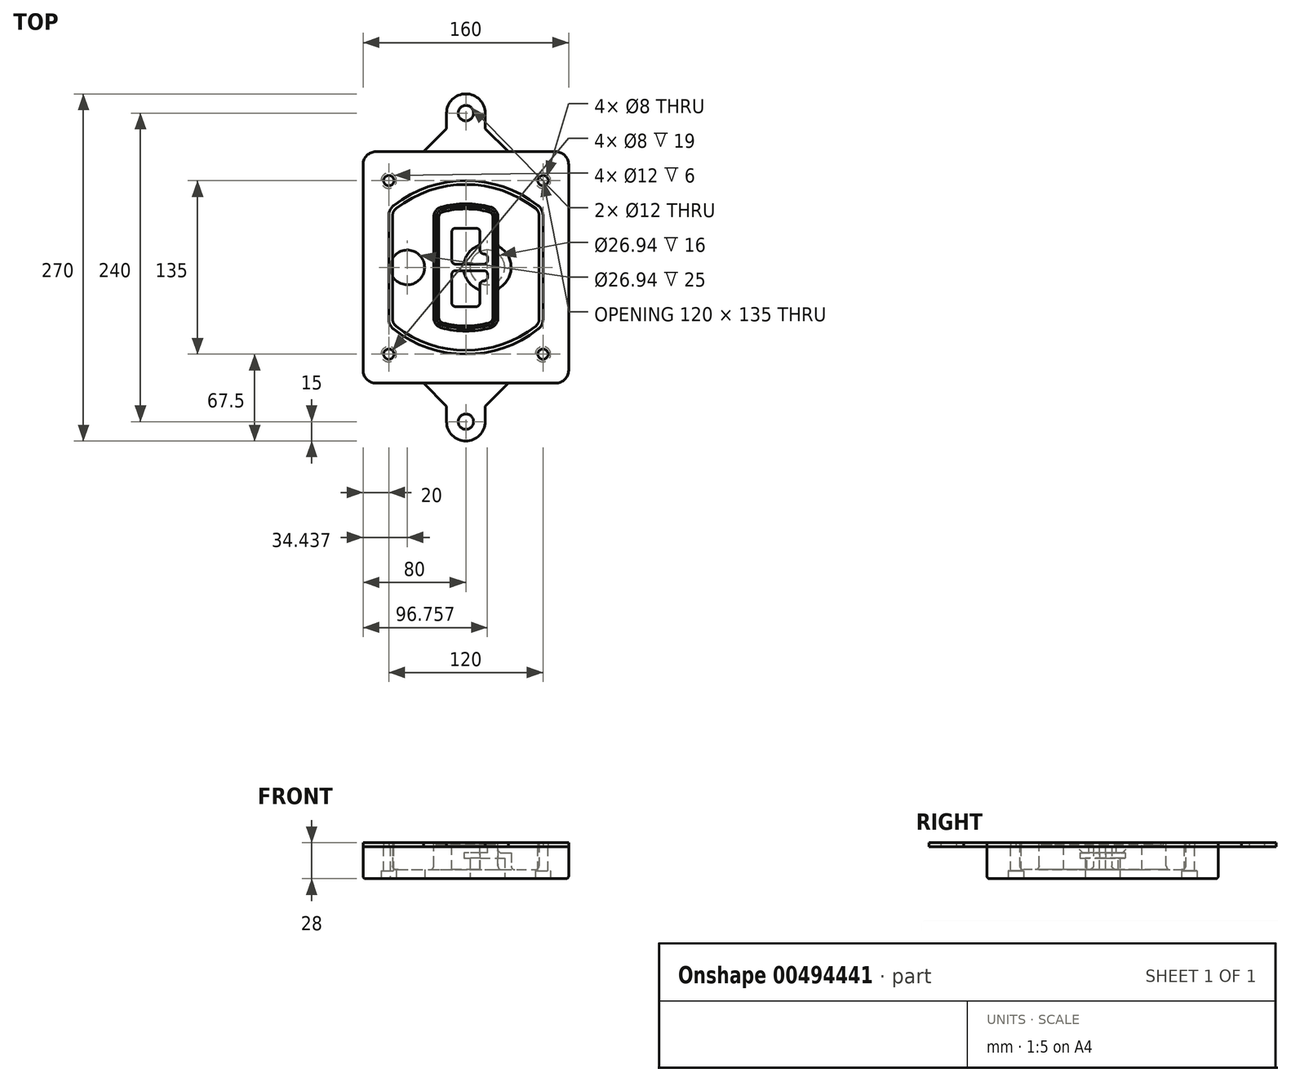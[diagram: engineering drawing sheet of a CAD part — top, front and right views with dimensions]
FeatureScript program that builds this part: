
annotation { "Feature Type Name" : "Feature", "Feature Type Description" : "" }
export const myFeature = defineFeature(function(context is Context, id is Id, definition is map)
    precondition{}
    {
        {
            var Q0;
            Q0=qCreatedBy(makeId("Top.planeOp"),FACE);
            var sketch = newSketch(context, id + "F0", { "sketchPlane" : qUnion([Q0])});
            skPoint(sketch, "E0.rect.middle", {"position": v(0, 0) * mm});
            skLineSegment(sketch, "E1.bottom", {"start": v(-70, -90) * mm, "end": v(70, -90) * mm});
            skLineSegment(sketch, "E1.top", {"start": v(-70, 90) * mm, "end": v(70, 90) * mm});
            skLineSegment(sketch, "E1.left", {"start": v(-80, -80) * mm, "end": v(-80, 80) * mm});
            skLineSegment(sketch, "E1.right", {"start": v(80, -80) * mm, "end": v(80, 80) * mm});
            skLineSegment(sketch, "E2", {"start": v(-80, 90) * mm, "end": v(80, -90) * mm, "construction": true});
            skLineSegment(sketch, "E3", {"start": v(80, 90) * mm, "end": v(-80, -90) * mm, "construction": true});
            skCircle(sketch, "E4", {"center": v(-60, 67.5) * mm, "radius": 4 * mm});
            skCircle(sketch, "E5", {"center": v(60, 67.5) * mm, "radius": 4 * mm});
            skCircle(sketch, "E6", {"center": v(60, -67.5) * mm, "radius": 4 * mm});
            skCircle(sketch, "E7", {"center": v(-60, -67.5) * mm, "radius": 4 * mm});
            skLineSegment(sketch, "E8", {"start": v(-60, 67.5) * mm, "end": v(60, 67.5) * mm, "construction": true});
            skLineSegment(sketch, "E9", {"start": v(60, 67.5) * mm, "end": v(60, -67.5) * mm, "construction": true});
            skLineSegment(sketch, "E10", {"start": v(60, -67.5) * mm, "end": v(-60, -67.5) * mm, "construction": true});
            skLineSegment(sketch, "E11", {"start": v(-60, -67.5) * mm, "end": v(-60, 67.5) * mm, "construction": true});
            skLineSegment(sketch, "E12", {"start": v(-60, 40.3) * mm, "end": v(-60, -40.3) * mm});
            skLineSegment(sketch, "E13", {"start": v(60, 40.3) * mm, "end": v(60, -40.3) * mm});
            skArc(sketch, "E14", {"start": v(56.15, 48.18) * mm, "mid": v(0, 67.5) * mm, "end": v(-56.15, 48.18) * mm});
            skArc(sketch, "E15", {"start": v(-56.15, -48.18) * mm, "mid": v(0, -67.5) * mm, "end": v(56.15, -48.18) * mm});
            skLineSegment(sketch, "E16", {"start": v(-60, 0) * mm, "end": v(60, 0) * mm, "construction": true});
            skPoint(sketch, "E17.visualSharp", {"position": v(-60, -45) * mm});
            skArc(sketch, "E17.filletArc", {"start": v(-60, -40.3) * mm, "mid": v(-58.99, -44.68) * mm, "end": v(-56.15, -48.18) * mm});
            skPoint(sketch, "E18.visualSharp", {"position": v(-60, 45) * mm});
            skArc(sketch, "E18.filletArc", {"start": v(-56.15, 48.18) * mm, "mid": v(-58.99, 44.68) * mm, "end": v(-60, 40.3) * mm});
            skPoint(sketch, "E19.visualSharp", {"position": v(60, 45) * mm});
            skArc(sketch, "E19.filletArc", {"start": v(60, 40.3) * mm, "mid": v(58.99, 44.68) * mm, "end": v(56.15, 48.18) * mm});
            skPoint(sketch, "E20.visualSharp", {"position": v(60, -45) * mm});
            skArc(sketch, "E20.filletArc", {"start": v(56.15, -48.18) * mm, "mid": v(58.99, -44.68) * mm, "end": v(60, -40.3) * mm});
            skPoint(sketch, "E21.visualSharp", {"position": v(-80, 90) * mm});
            skArc(sketch, "E21.filletArc", {"start": v(-70, 90) * mm, "mid": v(-77.07, 87.07) * mm, "end": v(-80, 80) * mm});
            skPoint(sketch, "E22.visualSharp", {"position": v(80, 90) * mm});
            skArc(sketch, "E22.filletArc", {"start": v(80, 80) * mm, "mid": v(77.07, 87.07) * mm, "end": v(70, 90) * mm});
            skPoint(sketch, "E23.visualSharp", {"position": v(80, -90) * mm});
            skArc(sketch, "E23.filletArc", {"start": v(70, -90) * mm, "mid": v(77.07, -87.07) * mm, "end": v(80, -80) * mm});
            skPoint(sketch, "E24.visualSharp", {"position": v(-80, -90) * mm});
            skArc(sketch, "E24.filletArc", {"start": v(-80, -80) * mm, "mid": v(-77.07, -87.07) * mm, "end": v(-70, -90) * mm});
            skArc(sketch, "E25.0", {"start": v(57, 40.3) * mm, "mid": v(56.3, 43.36) * mm, "end": v(54.3, 45.81) * mm});
            skLineSegment(sketch, "E25.1", {"start": v(57, 40.3) * mm, "end": v(57, -40.3) * mm});
            skArc(sketch, "E25.2", {"start": v(54.3, -45.81) * mm, "mid": v(56.3, -43.36) * mm, "end": v(57, -40.3) * mm});
            skArc(sketch, "E25.3", {"start": v(-54.3, -45.81) * mm, "mid": v(0, -64.5) * mm, "end": v(54.3, -45.81) * mm});
            skArc(sketch, "E25.4", {"start": v(-57, -40.3) * mm, "mid": v(-56.3, -43.36) * mm, "end": v(-54.3, -45.81) * mm});
            skArc(sketch, "E25.5", {"start": v(54.3, 45.81) * mm, "mid": v(0, 64.5) * mm, "end": v(-54.3, 45.81) * mm});
            skLineSegment(sketch, "E25.6", {"start": v(-57, 40.3) * mm, "end": v(-57, -40.3) * mm});
            skArc(sketch, "E25.7", {"start": v(-54.3, 45.81) * mm, "mid": v(-56.3, 43.36) * mm, "end": v(-57, 40.3) * mm});
            skArc(sketch, "E26.0", {"start": v(-58.62, 51.33) * mm, "mid": v(-62.58, 46.43) * mm, "end": v(-64, 40.3) * mm});
            skArc(sketch, "E26.1", {"start": v(58.62, 51.33) * mm, "mid": v(0, 71.5) * mm, "end": v(-58.62, 51.33) * mm});
            skArc(sketch, "E26.2", {"start": v(64, 40.3) * mm, "mid": v(62.58, 46.43) * mm, "end": v(58.62, 51.33) * mm});
            skLineSegment(sketch, "E26.3", {"start": v(64, 40.3) * mm, "end": v(64, -40.3) * mm});
            skArc(sketch, "E26.4", {"start": v(58.62, -51.33) * mm, "mid": v(62.58, -46.43) * mm, "end": v(64, -40.3) * mm});
            skLineSegment(sketch, "E26.5", {"start": v(-64, 40.3) * mm, "end": v(-64, -40.3) * mm});
            skArc(sketch, "E26.6", {"start": v(-58.62, -51.33) * mm, "mid": v(0, -71.5) * mm, "end": v(58.62, -51.33) * mm});
            skArc(sketch, "E26.7", {"start": v(-64, -40.3) * mm, "mid": v(-62.58, -46.43) * mm, "end": v(-58.62, -51.33) * mm});
            skSolve(sketch);
        }
        {
            var Q0;
            Q0=makeQuery(id+"F0.imprint","IMPRINT",FACE,{"disambiguationData":[TD([[makeQuery(id+"F0.imprint","IMPRINT",EDGE,{"derivedFrom":sQuery(id+"F0.wireOp",EDGE,"E1.bottom")}),1.0]])]});
            var Q1;
            Q1=makeQuery(id+"F0.imprint","IMPRINT",FACE,{"disambiguationData":[TD([[makeQuery(id+"F0.imprint","IMPRINT",EDGE,{"derivedFrom":sQuery(id+"F0.wireOp",EDGE,"E12")}),1.0]])]});
            var Q2;
            Q2=makeQuery(id+"F0.imprint","IMPRINT",FACE,{"disambiguationData":[TD([[makeQuery(id+"F0.imprint","IMPRINT",EDGE,{"derivedFrom":sQuery(id+"F0.wireOp",EDGE,"E25.0")}),1.0]])]});
            var Q3;
            Q3=makeQuery(id+"F0.imprint","IMPRINT",FACE,{"disambiguationData":[TD([[makeQuery(id+"F0.imprint","IMPRINT",EDGE,{"derivedFrom":sQuery(id+"F0.wireOp",EDGE,"E12")}),-1.0]])]});
            extrude(context, id + "F1", {"entities" : qUnion([Q0, Q1, Q2, Q3]), "oppositeDirection" : true, "depth" : 25 * mm});
        }
        {
            var Q0;
            Q0=makeQuery(id+"F0.imprint","IMPRINT",FACE,{"disambiguationData":[TD([[makeQuery(id+"F0.imprint","IMPRINT",EDGE,{"derivedFrom":sQuery(id+"F0.wireOp",EDGE,"E12")}),1.0]])]});
            extrude(context, id + "F2", {"entities" : qUnion([Q0]), "operationType" : NewBodyOperationType.ADD, "depth" : 3 * mm});
        }
        {
            var Q0;
            Q0=makeQuery(id+"F0.imprint","IMPRINT",FACE,{"disambiguationData":[TD([[makeQuery(id+"F0.imprint","IMPRINT",EDGE,{"derivedFrom":sQuery(id+"F0.wireOp",EDGE,"E25.0")}),1.0]])]});
            extrude(context, id + "F3", {"entities" : qUnion([Q0]), "operationType" : NewBodyOperationType.REMOVE, "oppositeDirection" : true, "depth" : 18 * mm});
        }
        {
            var Q0;
            Q0=makeQuery(id+"F2.opExtrude","CAP_FACE",FACE,{"disambiguationData":[OSD([sQuery(id+"F0.wireOp",EDGE,"E12"),sQuery(id+"F0.wireOp",EDGE,"E13"),sQuery(id+"F0.wireOp",EDGE,"E14"),sQuery(id+"F0.wireOp",EDGE,"E15"),sQuery(id+"F0.wireOp",EDGE,"E17.filletArc"),sQuery(id+"F0.wireOp",EDGE,"E18.filletArc"),sQuery(id+"F0.wireOp",EDGE,"E19.filletArc"),sQuery(id+"F0.wireOp",EDGE,"E20.filletArc"),sQuery(id+"F0.wireOp",EDGE,"E25.0"),sQuery(id+"F0.wireOp",EDGE,"E25.1"),sQuery(id+"F0.wireOp",EDGE,"E25.2"),sQuery(id+"F0.wireOp",EDGE,"E25.3"),sQuery(id+"F0.wireOp",EDGE,"E25.4"),sQuery(id+"F0.wireOp",EDGE,"E25.5"),sQuery(id+"F0.wireOp",EDGE,"E25.6"),sQuery(id+"F0.wireOp",EDGE,"E25.7")])],"isStart":false});
            var sketch = newSketch(context, id + "F4", { "sketchPlane" : qUnion([Q0])});
            skArc(sketch, "E27.0", {"start": v(-19.08, -46.97) * mm, "mid": v(0, -49.5) * mm, "end": v(19.08, -46.97) * mm});
            skArc(sketch, "E28.0", {"start": v(19.08, 46.97) * mm, "mid": v(0, 49.5) * mm, "end": v(-19.08, 46.97) * mm});
            skLineSegment(sketch, "E29", {"start": v(-25, 39.25) * mm, "end": v(-25, -39.25) * mm});
            skLineSegment(sketch, "E30", {"start": v(25, 39.25) * mm, "end": v(25, -39.25) * mm});
            skLineSegment(sketch, "E31", {"start": v(-25, 45.1) * mm, "end": v(25, 45.1) * mm, "construction": true});
            skLineSegment(sketch, "E32", {"start": v(-25, -45.1) * mm, "end": v(25, -45.1) * mm, "construction": true});
            skPoint(sketch, "E33.visualSharp", {"position": v(-25, 45.1) * mm});
            skArc(sketch, "E33.filletArc", {"start": v(-19.08, 46.97) * mm, "mid": v(-23.35, 44.11) * mm, "end": v(-25, 39.25) * mm});
            skPoint(sketch, "E34.visualSharp", {"position": v(25, 45.1) * mm});
            skArc(sketch, "E34.filletArc", {"start": v(25, 39.25) * mm, "mid": v(23.35, 44.11) * mm, "end": v(19.08, 46.97) * mm});
            skPoint(sketch, "E35.visualSharp", {"position": v(25, -45.1) * mm});
            skArc(sketch, "E35.filletArc", {"start": v(19.08, -46.97) * mm, "mid": v(23.35, -44.11) * mm, "end": v(25, -39.25) * mm});
            skPoint(sketch, "E36.visualSharp", {"position": v(-25, -45.1) * mm});
            skArc(sketch, "E36.filletArc", {"start": v(-25, -39.25) * mm, "mid": v(-23.35, -44.11) * mm, "end": v(-19.08, -46.97) * mm});
            skArc(sketch, "E37.0", {"start": v(54.3, 45.81) * mm, "mid": v(0, 64.5) * mm, "end": v(-54.3, 45.81) * mm});
            skArc(sketch, "E37.1", {"start": v(-54.3, 45.81) * mm, "mid": v(-56.3, 43.36) * mm, "end": v(-57, 40.3) * mm});
            skLineSegment(sketch, "E37.2", {"start": v(-57, 40.3) * mm, "end": v(-57, -40.3) * mm});
            skArc(sketch, "E37.3", {"start": v(-57, -40.3) * mm, "mid": v(-56.3, -43.36) * mm, "end": v(-54.3, -45.81) * mm});
            skArc(sketch, "E37.4", {"start": v(-54.3, -45.81) * mm, "mid": v(0, -64.5) * mm, "end": v(54.3, -45.81) * mm});
            skArc(sketch, "E37.5", {"start": v(54.3, -45.81) * mm, "mid": v(56.3, -43.36) * mm, "end": v(57, -40.3) * mm});
            skLineSegment(sketch, "E37.6", {"start": v(57, 40.3) * mm, "end": v(57, -40.3) * mm});
            skArc(sketch, "E37.7", {"start": v(57, 40.3) * mm, "mid": v(56.3, 43.36) * mm, "end": v(54.3, 45.81) * mm});
            skLineSegment(sketch, "E38.0", {"start": v(23, 39.25) * mm, "end": v(23, -39.25) * mm});
            skArc(sketch, "E38.1", {"start": v(18.56, -45.04) * mm, "mid": v(21.76, -42.9) * mm, "end": v(23, -39.25) * mm});
            skArc(sketch, "E38.2", {"start": v(-18.56, -45.04) * mm, "mid": v(0, -47.5) * mm, "end": v(18.56, -45.04) * mm});
            skArc(sketch, "E38.3", {"start": v(-23, -39.25) * mm, "mid": v(-21.76, -42.9) * mm, "end": v(-18.56, -45.04) * mm});
            skLineSegment(sketch, "E38.4", {"start": v(-23, 39.25) * mm, "end": v(-23, -39.25) * mm});
            skArc(sketch, "E38.5", {"start": v(23, 39.25) * mm, "mid": v(21.76, 42.9) * mm, "end": v(18.56, 45.04) * mm});
            skArc(sketch, "E38.6", {"start": v(-18.56, 45.04) * mm, "mid": v(-21.76, 42.9) * mm, "end": v(-23, 39.25) * mm});
            skArc(sketch, "E38.7", {"start": v(18.56, 45.04) * mm, "mid": v(0, 47.5) * mm, "end": v(-18.56, 45.04) * mm});
            skArc(sketch, "E39.0", {"start": v(21, 39.25) * mm, "mid": v(20.18, 41.68) * mm, "end": v(18.04, 43.1) * mm});
            skLineSegment(sketch, "E39.1", {"start": v(21, 39.25) * mm, "end": v(21, -39.25) * mm});
            skArc(sketch, "E39.2", {"start": v(18.04, -43.1) * mm, "mid": v(20.18, -41.68) * mm, "end": v(21, -39.25) * mm});
            skArc(sketch, "E39.3", {"start": v(-18.04, -43.1) * mm, "mid": v(0, -45.5) * mm, "end": v(18.04, -43.1) * mm});
            skArc(sketch, "E39.4", {"start": v(-21, -39.25) * mm, "mid": v(-20.18, -41.68) * mm, "end": v(-18.04, -43.1) * mm});
            skArc(sketch, "E39.5", {"start": v(18.04, 43.1) * mm, "mid": v(0, 45.5) * mm, "end": v(-18.04, 43.1) * mm});
            skLineSegment(sketch, "E39.6", {"start": v(-21, 39.25) * mm, "end": v(-21, -39.25) * mm});
            skArc(sketch, "E39.7", {"start": v(-18.04, 43.1) * mm, "mid": v(-20.18, 41.68) * mm, "end": v(-21, 39.25) * mm});
            skLineSegment(sketch, "E40", {"start": v(-25, 0) * mm, "end": v(25, 0) * mm, "construction": true});
            skLineSegment(sketch, "E41", {"start": v(-11, 5.5) * mm, "end": v(-11, 27.5) * mm});
            skLineSegment(sketch, "E42", {"start": v(-8, 30.5) * mm, "end": v(8, 30.5) * mm});
            skLineSegment(sketch, "E43", {"start": v(11, 27.5) * mm, "end": v(11, 13.5) * mm});
            skLineSegment(sketch, "E44", {"start": v(14, 10.5) * mm, "end": v(14, 10.5) * mm});
            skLineSegment(sketch, "E45", {"start": v(17, 7.5) * mm, "end": v(17, 5.5) * mm});
            skLineSegment(sketch, "E46", {"start": v(14, 2.5) * mm, "end": v(-8, 2.5) * mm});
            skPoint(sketch, "E47.visualSharp", {"position": v(-11, 30.5) * mm});
            skArc(sketch, "E47.filletArc", {"start": v(-8, 30.5) * mm, "mid": v(-10.12, 29.62) * mm, "end": v(-11, 27.5) * mm});
            skPoint(sketch, "E48.visualSharp", {"position": v(11, 30.5) * mm});
            skArc(sketch, "E48.filletArc", {"start": v(11, 27.5) * mm, "mid": v(10.12, 29.62) * mm, "end": v(8, 30.5) * mm});
            skPoint(sketch, "E49.visualSharp", {"position": v(11, 10.5) * mm});
            skArc(sketch, "E49.filletArc", {"start": v(11, 13.5) * mm, "mid": v(11.88, 11.38) * mm, "end": v(14, 10.5) * mm});
            skPoint(sketch, "E50.visualSharp", {"position": v(17, 10.5) * mm});
            skArc(sketch, "E50.filletArc", {"start": v(17, 7.5) * mm, "mid": v(16.12, 9.62) * mm, "end": v(14, 10.5) * mm});
            skPoint(sketch, "E51.visualSharp", {"position": v(17, 2.5) * mm});
            skArc(sketch, "E51.filletArc", {"start": v(14, 2.5) * mm, "mid": v(16.12, 3.38) * mm, "end": v(17, 5.5) * mm});
            skPoint(sketch, "E52.visualSharp", {"position": v(-11, 2.5) * mm});
            skArc(sketch, "E52.filletArc", {"start": v(-11, 5.5) * mm, "mid": v(-10.12, 3.38) * mm, "end": v(-8, 2.5) * mm});
            skLineSegment(sketch, "E53.0.MirrorCS", {"start": v(14, -2.5) * mm, "end": v(-8, -2.5) * mm});
            skArc(sketch, "E54.0.MirrorCS", {"start": v(-11, -5.5) * mm, "mid": v(-10.12, -3.38) * mm, "end": v(-8, -2.5) * mm});
            skLineSegment(sketch, "E55.0.MirrorCS", {"start": v(-11, -5.5) * mm, "end": v(-11, -27.5) * mm});
            skArc(sketch, "E56.0.MirrorCS", {"start": v(-8, -30.5) * mm, "mid": v(-10.12, -29.62) * mm, "end": v(-11, -27.5) * mm});
            skLineSegment(sketch, "E57.0.MirrorCS", {"start": v(-8, -30.5) * mm, "end": v(8, -30.5) * mm});
            skArc(sketch, "E58.0.MirrorCS", {"start": v(11, -27.5) * mm, "mid": v(10.12, -29.62) * mm, "end": v(8, -30.5) * mm});
            skLineSegment(sketch, "E59.0.MirrorCS", {"start": v(11, -27.5) * mm, "end": v(11, -13.5) * mm});
            skArc(sketch, "E60.0.MirrorCS", {"start": v(11, -13.5) * mm, "mid": v(11.88, -11.38) * mm, "end": v(14, -10.5) * mm});
            skArc(sketch, "E61.0.MirrorCS", {"start": v(17, -7.5) * mm, "mid": v(16.12, -9.62) * mm, "end": v(14, -10.5) * mm});
            skLineSegment(sketch, "E62.0.MirrorCS", {"start": v(17, -7.5) * mm, "end": v(17, -5.5) * mm});
            skArc(sketch, "E63.0.MirrorCS", {"start": v(14, -2.5) * mm, "mid": v(16.12, -3.38) * mm, "end": v(17, -5.5) * mm});
            skSolve(sketch);
        }
        {
            var Q0;
            Q0=makeQuery(id+"F4.imprint","IMPRINT",FACE,{"disambiguationData":[TD([[makeQuery(id+"F4.imprint","IMPRINT",EDGE,{"derivedFrom":sQuery(id+"F4.wireOp",EDGE,"E27.0")}),1.0]])]});
            var Q1;
            Q1=makeQuery(id+"F4.imprint","IMPRINT",FACE,{"disambiguationData":[TD([[makeQuery(id+"F4.imprint","IMPRINT",EDGE,{"derivedFrom":sQuery(id+"F4.wireOp",EDGE,"E38.0")}),-1.0]])]});
            var Q2;
            Q2=makeQuery(id+"F4.imprint","IMPRINT",FACE,{"disambiguationData":[TD([[makeQuery(id+"F4.imprint","IMPRINT",EDGE,{"derivedFrom":sQuery(id+"F4.wireOp",EDGE,"E39.0")}),1.0]])]});
            extrude(context, id + "F5", {"entities" : qUnion([Q0, Q1, Q2]), "operationType" : NewBodyOperationType.ADD, "endBound" : BoundingType.UP_TO_NEXT, "oppositeDirection" : true, "depth" : 25 * mm});
        }
        {
            var Q0;
            Q0=makeQuery(id+"F4.imprint","IMPRINT",FACE,{"disambiguationData":[TD([[makeQuery(id+"F4.imprint","IMPRINT",EDGE,{"derivedFrom":sQuery(id+"F4.wireOp",EDGE,"E38.0")}),-1.0]])]});
            extrude(context, id + "F6", {"entities" : qUnion([Q0]), "operationType" : NewBodyOperationType.REMOVE, "oppositeDirection" : true, "depth" : 2 * mm});
        }
        {
            var Q0;
            Q0=makeQuery(id+"F1.opExtrude","CAP_FACE",FACE,{"disambiguationData":[OSD([sQuery(id+"F0.wireOp",EDGE,"E1.bottom"),sQuery(id+"F0.wireOp",EDGE,"E1.top"),sQuery(id+"F0.wireOp",EDGE,"E1.left"),sQuery(id+"F0.wireOp",EDGE,"E1.right"),sQuery(id+"F0.wireOp",EDGE,"E4"),sQuery(id+"F0.wireOp",EDGE,"E5"),sQuery(id+"F0.wireOp",EDGE,"E6"),sQuery(id+"F0.wireOp",EDGE,"E7"),sQuery(id+"F0.wireOp",EDGE,"E21.filletArc"),sQuery(id+"F0.wireOp",EDGE,"E22.filletArc"),sQuery(id+"F0.wireOp",EDGE,"E23.filletArc"),sQuery(id+"F0.wireOp",EDGE,"E24.filletArc")])],"isStart":false});
            var sketch = newSketch(context, id + "F7", { "sketchPlane" : qUnion([Q0])});
            skCircle(sketch, "E64", {"center": v(16.76, 0) * mm, "radius": 13.47 * mm});
            skCircle(sketch, "E65", {"center": v(-45.56, 0) * mm, "radius": 13.47 * mm});
            skLineSegment(sketch, "E66", {"start": v(80, 0) * mm, "end": v(-80, 0) * mm});
            skCircle(sketch, "E67", {"center": v(16.76, 0) * mm, "radius": 18.47 * mm});
            skCircle(sketch, "E68", {"center": v(60, -67.5) * mm, "radius": 6 * mm});
            skCircle(sketch, "E69", {"center": v(-60, -67.5) * mm, "radius": 6 * mm});
            skCircle(sketch, "E70", {"center": v(-60, 67.5) * mm, "radius": 6 * mm});
            skCircle(sketch, "E71", {"center": v(60, 67.5) * mm, "radius": 6 * mm});
            skSolve(sketch);
        }
        {
            var Q0;
            {var subQ1=sQuery(id+"F7.wireOp",EDGE,"E66");var subQ4=sQuery(id+"F7.wireOp",EDGE,"E64");var subQ6=makeQuery(id+"F7.imprint","INTERSECT",VERTEX,{"disambiguationData":[OD(0.0)],"derivedFrom":[subQ4,subQ1]});Q0=makeQuery(id+"F7.imprint","IMPRINT",FACE,{"disambiguationData":[TD([[makeQuery(id+"F7.imprint","IMPRINT",EDGE,{"disambiguationData":[TD([[subQ6,-1.0]])],"derivedFrom":subQ4}),-1.0]])]});}
            var Q1;
            {var subQ0=sQuery(id+"F7.wireOp",EDGE,"E66");var subQ1=sQuery(id+"F7.wireOp",EDGE,"E64");var subQ3=makeQuery(id+"F7.imprint","INTERSECT",VERTEX,{"disambiguationData":[OD(0.0)],"derivedFrom":[subQ1,subQ0]});Q1=makeQuery(id+"F7.imprint","IMPRINT",FACE,{"disambiguationData":[TD([[makeQuery(id+"F7.imprint","IMPRINT",EDGE,{"disambiguationData":[TD([[subQ3,-1.0]])],"derivedFrom":subQ1}),1.0]])]});}
            var Q2;
            {var subQ0=sQuery(id+"F7.wireOp",EDGE,"E66");var subQ1=sQuery(id+"F7.wireOp",EDGE,"E64");var subQ3=makeQuery(id+"F7.imprint","INTERSECT",VERTEX,{"disambiguationData":[OD(0.0)],"derivedFrom":[subQ1,subQ0]});Q2=makeQuery(id+"F7.imprint","IMPRINT",FACE,{"disambiguationData":[TD([[makeQuery(id+"F7.imprint","IMPRINT",EDGE,{"disambiguationData":[TD([[subQ3,1.0]])],"derivedFrom":subQ1}),1.0]])]});}
            var Q3;
            {var subQ1=sQuery(id+"F7.wireOp",EDGE,"E66");var subQ4=sQuery(id+"F7.wireOp",EDGE,"E64");var subQ6=makeQuery(id+"F7.imprint","INTERSECT",VERTEX,{"disambiguationData":[OD(0.0)],"derivedFrom":[subQ4,subQ1]});Q3=makeQuery(id+"F7.imprint","IMPRINT",FACE,{"disambiguationData":[TD([[makeQuery(id+"F7.imprint","IMPRINT",EDGE,{"disambiguationData":[TD([[subQ6,1.0]])],"derivedFrom":subQ4}),-1.0]])]});}
            extrude(context, id + "F8", {"entities" : qUnion([Q0, Q1, Q2, Q3]), "operationType" : NewBodyOperationType.ADD, "oppositeDirection" : true, "depth" : 20 * mm});
        }
        {
            var Q0;
            {var subQ0=sQuery(id+"F7.wireOp",EDGE,"E66");var subQ1=sQuery(id+"F7.wireOp",EDGE,"E64");var subQ3=makeQuery(id+"F7.imprint","INTERSECT",VERTEX,{"disambiguationData":[OD(0.0)],"derivedFrom":[subQ1,subQ0]});Q0=makeQuery(id+"F7.imprint","IMPRINT",FACE,{"disambiguationData":[TD([[makeQuery(id+"F7.imprint","IMPRINT",EDGE,{"disambiguationData":[TD([[subQ3,-1.0]])],"derivedFrom":subQ1}),1.0]])]});}
            var Q1;
            {var subQ0=sQuery(id+"F7.wireOp",EDGE,"E66");var subQ1=sQuery(id+"F7.wireOp",EDGE,"E64");var subQ3=makeQuery(id+"F7.imprint","INTERSECT",VERTEX,{"disambiguationData":[OD(0.0)],"derivedFrom":[subQ1,subQ0]});Q1=makeQuery(id+"F7.imprint","IMPRINT",FACE,{"disambiguationData":[TD([[makeQuery(id+"F7.imprint","IMPRINT",EDGE,{"disambiguationData":[TD([[subQ3,1.0]])],"derivedFrom":subQ1}),1.0]])]});}
            extrude(context, id + "F9", {"entities" : qUnion([Q0, Q1]), "operationType" : NewBodyOperationType.REMOVE, "oppositeDirection" : true, "depth" : 16 * mm});
        }
        {
            var Q0;
            {var subQ0=sQuery(id+"F7.wireOp",EDGE,"E66");var subQ1=sQuery(id+"F7.wireOp",EDGE,"E65");var subQ3=makeQuery(id+"F7.imprint","INTERSECT",VERTEX,{"disambiguationData":[OD(0.0)],"derivedFrom":[subQ1,subQ0]});Q0=makeQuery(id+"F7.imprint","IMPRINT",FACE,{"disambiguationData":[TD([[makeQuery(id+"F7.imprint","IMPRINT",EDGE,{"disambiguationData":[TD([[subQ3,-1.0]])],"derivedFrom":subQ1}),1.0]])]});}
            var Q1;
            {var subQ0=sQuery(id+"F7.wireOp",EDGE,"E66");var subQ1=sQuery(id+"F7.wireOp",EDGE,"E65");var subQ3=makeQuery(id+"F7.imprint","INTERSECT",VERTEX,{"disambiguationData":[OD(0.0)],"derivedFrom":[subQ1,subQ0]});Q1=makeQuery(id+"F7.imprint","IMPRINT",FACE,{"disambiguationData":[TD([[makeQuery(id+"F7.imprint","IMPRINT",EDGE,{"disambiguationData":[TD([[subQ3,1.0]])],"derivedFrom":subQ1}),1.0]])]});}
            extrude(context, id + "F10", {"entities" : qUnion([Q0, Q1]), "operationType" : NewBodyOperationType.REMOVE, "oppositeDirection" : true, "depth" : 25 * mm});
        }
        {
            var Q0;
            Q0=makeQuery(id+"F7.imprint","IMPRINT",FACE,{"disambiguationData":[TD([[makeQuery(id+"F7.imprint","IMPRINT",EDGE,{"derivedFrom":sQuery(id+"F7.wireOp",EDGE,"E68")}),1.0]])]});
            var Q1;
            Q1=makeQuery(id+"F7.imprint","IMPRINT",FACE,{"disambiguationData":[TD([[makeQuery(id+"F7.imprint","IMPRINT",EDGE,{"derivedFrom":makeQuery(id+"F1.opExtrude","CAP_EDGE",EDGE,{"disambiguationData":[OSD([sQuery(id+"F0.wireOp",EDGE,"E5")])],"isStart":false})}),-1.0]])]});
            var Q2;
            Q2=makeQuery(id+"F7.imprint","IMPRINT",FACE,{"disambiguationData":[TD([[makeQuery(id+"F7.imprint","IMPRINT",EDGE,{"derivedFrom":sQuery(id+"F7.wireOp",EDGE,"E69")}),1.0]])]});
            var Q3;
            Q3=makeQuery(id+"F7.imprint","IMPRINT",FACE,{"disambiguationData":[TD([[makeQuery(id+"F7.imprint","IMPRINT",EDGE,{"derivedFrom":makeQuery(id+"F1.opExtrude","CAP_EDGE",EDGE,{"disambiguationData":[OSD([sQuery(id+"F0.wireOp",EDGE,"E4")])],"isStart":false})}),-1.0]])]});
            var Q4;
            Q4=makeQuery(id+"F7.imprint","IMPRINT",FACE,{"disambiguationData":[TD([[makeQuery(id+"F7.imprint","IMPRINT",EDGE,{"derivedFrom":sQuery(id+"F7.wireOp",EDGE,"E70")}),1.0]])]});
            var Q5;
            Q5=makeQuery(id+"F7.imprint","IMPRINT",FACE,{"disambiguationData":[TD([[makeQuery(id+"F7.imprint","IMPRINT",EDGE,{"derivedFrom":makeQuery(id+"F1.opExtrude","CAP_EDGE",EDGE,{"disambiguationData":[OSD([sQuery(id+"F0.wireOp",EDGE,"E7")])],"isStart":false})}),-1.0]])]});
            var Q6;
            Q6=makeQuery(id+"F7.imprint","IMPRINT",FACE,{"disambiguationData":[TD([[makeQuery(id+"F7.imprint","IMPRINT",EDGE,{"derivedFrom":sQuery(id+"F7.wireOp",EDGE,"E71")}),1.0]])]});
            var Q7;
            Q7=makeQuery(id+"F7.imprint","IMPRINT",FACE,{"disambiguationData":[TD([[makeQuery(id+"F7.imprint","IMPRINT",EDGE,{"derivedFrom":makeQuery(id+"F1.opExtrude","CAP_EDGE",EDGE,{"disambiguationData":[OSD([sQuery(id+"F0.wireOp",EDGE,"E6")])],"isStart":false})}),-1.0]])]});
            extrude(context, id + "F11", {"entities" : qUnion([Q0, Q1, Q2, Q3, Q4, Q5, Q6, Q7]), "operationType" : NewBodyOperationType.REMOVE, "oppositeDirection" : true, "depth" : 6 * mm});
        }
        {
            var Q0;
            Q0=makeQuery(id+"F9.boolean.opBoolean","COPY",FACE,{"derivedFrom":makeQuery(id+"F9.opExtrude","CAP_FACE",FACE,{"disambiguationData":[OSD([sQuery(id+"F7.wireOp",EDGE,"E64")])],"isStart":false})});
            var sketch = newSketch(context, id + "F12", { "sketchPlane" : qUnion([Q0])});
            skArc(sketch, "E72.0", {"start": v(11, 17.55) * mm, "mid": v(2.57, 11.82) * mm, "end": v(-1.54, 2.5) * mm});
            skArc(sketch, "E72.1", {"start": v(-1.54, -2.5) * mm, "mid": v(2.57, -11.82) * mm, "end": v(11, -17.55) * mm});
            skLineSegment(sketch, "E73", {"start": v(-1.54, -2.5) * mm, "end": v(14, -2.5) * mm});
            skLineSegment(sketch, "E74.0", {"start": v(14, 2.5) * mm, "end": v(-1.54, 2.5) * mm});
            skArc(sketch, "E74.1", {"start": v(14, 2.5) * mm, "mid": v(16.12, 3.38) * mm, "end": v(17, 5.5) * mm});
            skLineSegment(sketch, "E74.2", {"start": v(17, 7.5) * mm, "end": v(17, 5.5) * mm});
            skArc(sketch, "E74.3", {"start": v(17, 7.5) * mm, "mid": v(16.12, 9.62) * mm, "end": v(14, 10.5) * mm});
            skArc(sketch, "E74.4", {"start": v(11, 13.5) * mm, "mid": v(11.88, 11.38) * mm, "end": v(14, 10.5) * mm});
            skLineSegment(sketch, "E74.5", {"start": v(11, 17.55) * mm, "end": v(11, 13.5) * mm});
            skLineSegment(sketch, "E74.7", {"start": v(14, -2.5) * mm, "end": v(-1.54, -2.5) * mm});
            skArc(sketch, "E74.8", {"start": v(14, -2.5) * mm, "mid": v(16.12, -3.38) * mm, "end": v(17, -5.5) * mm});
            skLineSegment(sketch, "E74.9", {"start": v(17, -7.5) * mm, "end": v(17, -5.5) * mm});
            skArc(sketch, "E74.10", {"start": v(17, -7.5) * mm, "mid": v(16.12, -9.62) * mm, "end": v(14, -10.5) * mm});
            skArc(sketch, "E74.11", {"start": v(11, -13.5) * mm, "mid": v(11.88, -11.38) * mm, "end": v(14, -10.5) * mm});
            skLineSegment(sketch, "E74.12", {"start": v(11, -17.55) * mm, "end": v(11, -13.5) * mm});
            skPoint(sketch, "E75.orphan", {"position": v(11, -27.5) * mm});
            skPoint(sketch, "E76.orphan", {"position": v(-8, -2.5) * mm});
            skPoint(sketch, "E77.orphan", {"position": v(-8, 2.5) * mm});
            skPoint(sketch, "E78.orphan", {"position": v(11, 27.5) * mm});
            skSolve(sketch);
        }
        {
            var Q0;
            {var subQ7=sQuery(id+"F12.wireOp",EDGE,"E72.0");var subQ14=sQuery(id+"F12.wireOp",EDGE,"E72.1");var subQ16=sQuery(id+"F12.wireOp",EDGE,"E74.1");var subQ18=sQuery(id+"F12.wireOp",EDGE,"E74.8");Q0=qUnion([makeQuery(id+"F12.imprint","IMPRINT",FACE,{"disambiguationData":[TD([[makeQuery(id+"F12.imprint","IMPRINT",EDGE,{"derivedFrom":subQ7}),1.0]])]}),makeQuery(id+"F12.imprint","IMPRINT",FACE,{"disambiguationData":[TD([[makeQuery(id+"F12.imprint","IMPRINT",EDGE,{"derivedFrom":subQ14}),1.0]])]}),makeQuery(id+"F12.imprint","IMPRINT",FACE,{"disambiguationData":[TD([[makeQuery(id+"F12.imprint","IMPRINT",EDGE,{"derivedFrom":subQ16}),1.0]])]}),makeQuery(id+"F12.imprint","IMPRINT",FACE,{"disambiguationData":[TD([[makeQuery(id+"F12.imprint","IMPRINT",EDGE,{"derivedFrom":subQ18}),-1.0]])]})]);}
            var Q1;
            Q1=makeQuery(id+"F5.boolean.opBoolean","SPLIT",FACE,{"disambiguationData":[TD([makeQuery(id+"F5.opExtrude","SWEPT_FACE",FACE,{"disambiguationData":[OSD([sQuery(id+"F4.wireOp",EDGE,"E41")])]})])],"derivedFrom":makeQuery(id+"F3.boolean.opBoolean","COPY",FACE,{"derivedFrom":makeQuery(id+"F3.opExtrude","CAP_FACE",FACE,{"disambiguationData":[OSD([sQuery(id+"F0.wireOp",EDGE,"E25.0"),sQuery(id+"F0.wireOp",EDGE,"E25.1"),sQuery(id+"F0.wireOp",EDGE,"E25.2"),sQuery(id+"F0.wireOp",EDGE,"E25.3"),sQuery(id+"F0.wireOp",EDGE,"E25.4"),sQuery(id+"F0.wireOp",EDGE,"E25.5"),sQuery(id+"F0.wireOp",EDGE,"E25.6"),sQuery(id+"F0.wireOp",EDGE,"E25.7")])],"isStart":false})})});
            extrude(context, id + "F13", {"entities" : qUnion([Q0]), "operationType" : NewBodyOperationType.REMOVE, "endBound" : BoundingType.UP_TO_SURFACE, "endBoundEntityFace" : qUnion([Q1]), "depth" : 25 * mm});
        }
        {
            var Q0;
            Q0=makeQuery(id+"F3.boolean.opBoolean","COPY",EDGE,{"derivedFrom":makeQuery(id+"F3.opExtrude","CAP_EDGE",EDGE,{"disambiguationData":[OSD([sQuery(id+"F0.wireOp",EDGE,"E25.6")])],"isStart":false})});
            var Q1;
            Q1=makeQuery(id+"F8.boolean.opBoolean","INTERSECT",EDGE,{"derivedFrom":[makeQuery(id+"F5.opExtrude","SWEPT_FACE",FACE,{"disambiguationData":[OSD([sQuery(id+"F4.wireOp",EDGE,"E30")])]}),makeQuery(id+"F8.opExtrude","CAP_FACE",FACE,{"disambiguationData":[OSD([sQuery(id+"F7.wireOp",EDGE,"E67")])],"isStart":false})]});
            var Q2;
            Q2=makeQuery(id+"F8.boolean.opBoolean","INTERSECT",EDGE,{"disambiguationData":[OD(1.0)],"derivedFrom":[makeQuery(id+"F5.opExtrude","SWEPT_FACE",FACE,{"disambiguationData":[OSD([sQuery(id+"F4.wireOp",EDGE,"E30")])]}),makeQuery(id+"F8.opExtrude","SWEPT_FACE",FACE,{"disambiguationData":[OSD([sQuery(id+"F7.wireOp",EDGE,"E67")])]})]});
            var Q3;
            {var subQ0=sQuery(id+"F4.wireOp",EDGE,"E30");Q3=makeQuery(id+"F8.boolean.opBoolean","SPLIT",EDGE,{"disambiguationData":[TD([makeQuery(id+"F5.opExtrude","SWEPT_FACE",FACE,{"disambiguationData":[OSD([sQuery(id+"F4.wireOp",EDGE,"E35.filletArc")])]})])],"derivedFrom":makeQuery(id+"F5.opExtrude","CAP_EDGE",EDGE,{"disambiguationData":[OSD([subQ0])],"isStart":false})});}
            var Q4;
            {var subQ0=sQuery(id+"F0.wireOp",EDGE,"E25.7");var subQ1=sQuery(id+"F0.wireOp",EDGE,"E25.1");var subQ2=sQuery(id+"F0.wireOp",EDGE,"E25.6");var subQ3=sQuery(id+"F0.wireOp",EDGE,"E25.5");var subQ4=sQuery(id+"F0.wireOp",EDGE,"E25.4");var subQ5=sQuery(id+"F0.wireOp",EDGE,"E25.0");var subQ6=sQuery(id+"F0.wireOp",EDGE,"E25.2");var subQ7=sQuery(id+"F0.wireOp",EDGE,"E25.3");Q4=makeQuery(id+"F8.boolean.opBoolean","INTERSECT",EDGE,{"derivedFrom":[makeQuery(id+"F5.boolean.opBoolean","SPLIT",FACE,{"disambiguationData":[TD([makeQuery(id+"F2.opExtrude","SWEPT_FACE",FACE,{"disambiguationData":[OSD([subQ5])]})])],"derivedFrom":makeQuery(id+"F3.boolean.opBoolean","COPY",FACE,{"derivedFrom":makeQuery(id+"F3.opExtrude","CAP_FACE",FACE,{"disambiguationData":[OSD([subQ5,subQ1,subQ6,subQ7,subQ4,subQ3,subQ2,subQ0])],"isStart":false})})}),makeQuery(id+"F8.opExtrude","SWEPT_FACE",FACE,{"disambiguationData":[OSD([sQuery(id+"F7.wireOp",EDGE,"E67")])]})]});}
            var Q5;
            Q5=makeQuery(id+"F8.boolean.opBoolean","INTERSECT",EDGE,{"disambiguationData":[OD(0.0)],"derivedFrom":[makeQuery(id+"F5.opExtrude","SWEPT_FACE",FACE,{"disambiguationData":[OSD([sQuery(id+"F4.wireOp",EDGE,"E30")])]}),makeQuery(id+"F8.opExtrude","SWEPT_FACE",FACE,{"disambiguationData":[OSD([sQuery(id+"F7.wireOp",EDGE,"E67")])]})]});
            fillet(context, id + "F14", {"entities" : qUnion([Q0, Q1, Q2, Q3, Q4, Q5]), "radius" : 3 * mm, "tangentPropagation" : true, "allowEdgeOverflow" : false});
        }
        {
            var Q0;
            Q0=makeQuery(id+"F1.opExtrude","CAP_EDGE",EDGE,{"disambiguationData":[OSD([sQuery(id+"F0.wireOp",EDGE,"E1.bottom")])],"isStart":false});
            fillet(context, id + "F15", {"entities" : qUnion([Q0]), "radius" : 2 * mm, "tangentPropagation" : true, "allowEdgeOverflow" : false});
        }
        {
            var Q0;
            Q0=makeQuery(id+"F0.imprint","IMPRINT",FACE,{"disambiguationData":[TD([[makeQuery(id+"F0.imprint","IMPRINT",EDGE,{"derivedFrom":sQuery(id+"F0.wireOp",EDGE,"E1.bottom")}),1.0]])]});
            var sketch = newSketch(context, id + "F16", { "sketchPlane" : qUnion([Q0])});
            skCircle(sketch, "E79", {"center": v(0, 120) * mm, "radius": 6 * mm});
            skLineSegment(sketch, "E80", {"start": v(-33, 90) * mm, "end": v(-15, 108) * mm});
            skLineSegment(sketch, "E81", {"start": v(33, 90) * mm, "end": v(15, 108) * mm});
            skLineSegment(sketch, "E82", {"start": v(15, 108) * mm, "end": v(15, 120) * mm});
            skLineSegment(sketch, "E83", {"start": v(-15, 108) * mm, "end": v(-15, 120) * mm});
            skArc(sketch, "E84", {"start": v(15, 120) * mm, "mid": v(0, 135) * mm, "end": v(-15, 120) * mm});
            skLineSegment(sketch, "E85", {"start": v(-74.18, 0) * mm, "end": v(74.01, 0) * mm, "construction": true});
            skLineSegment(sketch, "E86.MirrorCS", {"start": v(15, -108) * mm, "end": v(15, -120) * mm});
            skLineSegment(sketch, "E87.MirrorCS", {"start": v(0, -90) * mm, "end": v(0, -120) * mm, "construction": true});
            skLineSegment(sketch, "E88.MirrorCS", {"start": v(33, -90) * mm, "end": v(15, -108) * mm});
            skLineSegment(sketch, "E89.MirrorCS", {"start": v(-15, -108) * mm, "end": v(-15, -120) * mm});
            skArc(sketch, "E90.MirrorCS", {"start": v(15, -120) * mm, "mid": v(0, -135) * mm, "end": v(-15, -120) * mm});
            skCircle(sketch, "E91.MirrorC", {"center": v(0, -120) * mm, "radius": 6 * mm});
            skLineSegment(sketch, "E92.MirrorCS", {"start": v(-33, -90) * mm, "end": v(-15, -108) * mm});
            skLineSegment(sketch, "E93", {"start": v(0, 90) * mm, "end": v(0, 120) * mm, "construction": true});
            skLineSegment(sketch, "E94", {"start": v(-33, 90) * mm, "end": v(33, 90) * mm});
            skLineSegment(sketch, "E95", {"start": v(-33, -90) * mm, "end": v(33, -90) * mm});
            skSolve(sketch);
        }
        {
            var Q0;
            Q0 = qSketchRegion(id + "F16", true);
            var Q1;
            Q1=makeQuery(id+"F0.imprint","IMPRINT",FACE,{"disambiguationData":[TD([[makeQuery(id+"F0.imprint","IMPRINT",EDGE,{"derivedFrom":sQuery(id+"F0.wireOp",EDGE,"E12")}),-1.0]])]});
            var Q2;
            Q2=makeQuery(id+"F0.imprint","IMPRINT",FACE,{"disambiguationData":[TD([[makeQuery(id+"F0.imprint","IMPRINT",EDGE,{"derivedFrom":sQuery(id+"F0.wireOp",EDGE,"E1.bottom")}),1.0]])]});
            var Q3;
            Q3=makeQuery(id+"F2.opExtrude","CAP_FACE",FACE,{"disambiguationData":[OSD([sQuery(id+"F0.wireOp",EDGE,"E12"),sQuery(id+"F0.wireOp",EDGE,"E13"),sQuery(id+"F0.wireOp",EDGE,"E14"),sQuery(id+"F0.wireOp",EDGE,"E15"),sQuery(id+"F0.wireOp",EDGE,"E17.filletArc"),sQuery(id+"F0.wireOp",EDGE,"E18.filletArc"),sQuery(id+"F0.wireOp",EDGE,"E19.filletArc"),sQuery(id+"F0.wireOp",EDGE,"E20.filletArc"),sQuery(id+"F0.wireOp",EDGE,"E25.0"),sQuery(id+"F0.wireOp",EDGE,"E25.1"),sQuery(id+"F0.wireOp",EDGE,"E25.2"),sQuery(id+"F0.wireOp",EDGE,"E25.3"),sQuery(id+"F0.wireOp",EDGE,"E25.4"),sQuery(id+"F0.wireOp",EDGE,"E25.5"),sQuery(id+"F0.wireOp",EDGE,"E25.6"),sQuery(id+"F0.wireOp",EDGE,"E25.7")])],"isStart":false});
            extrude(context, id + "F17", {"entities" : qUnion([Q0, Q1, Q2]), "endBound" : BoundingType.UP_TO_SURFACE, "endBoundEntityFace" : qUnion([Q3]), "depth" : 25 * mm});
        }
    });
